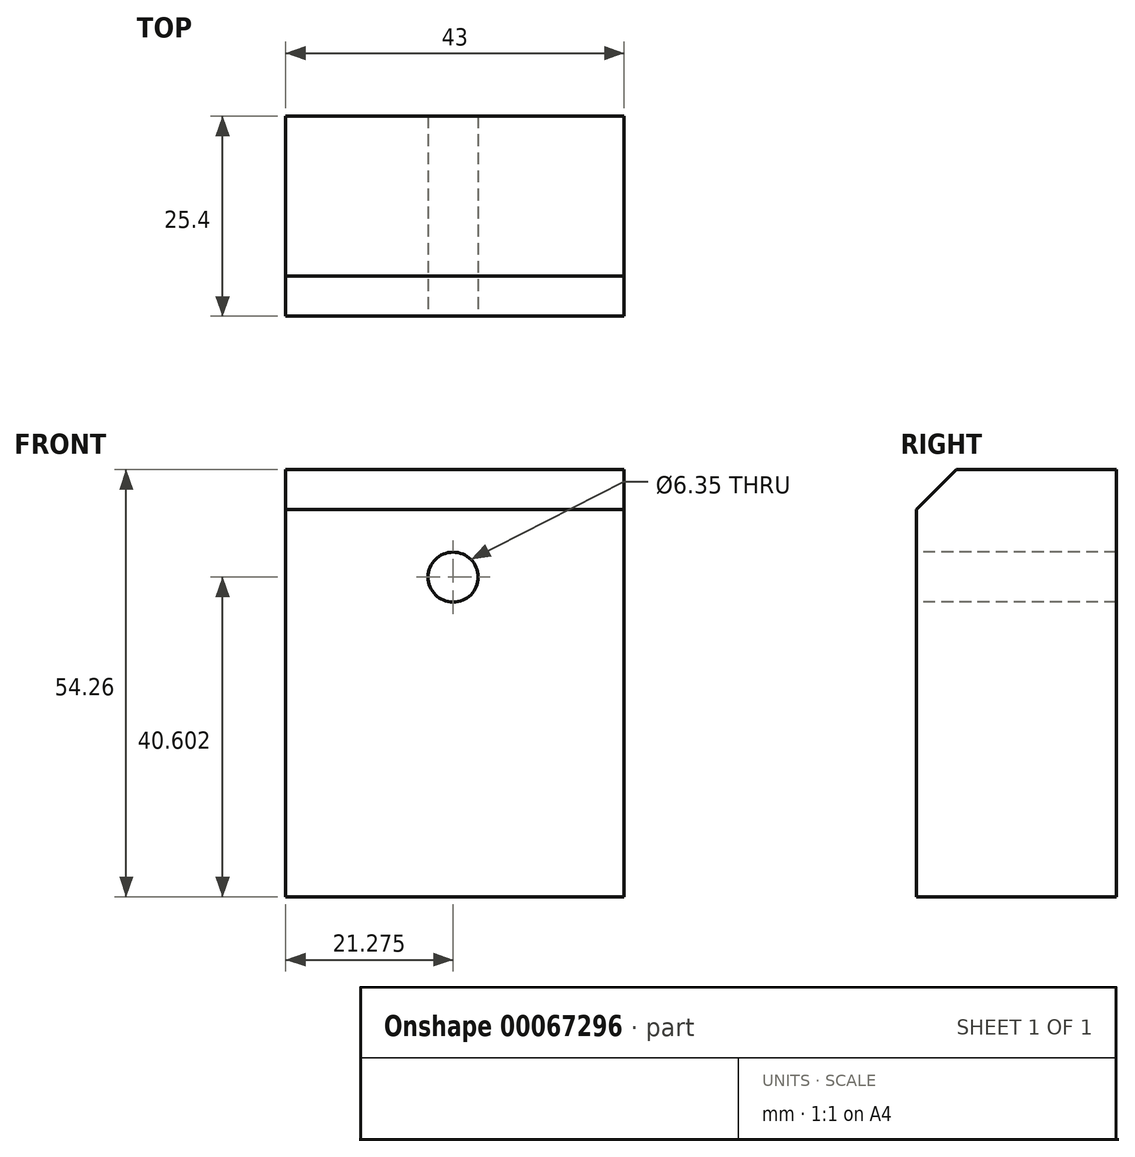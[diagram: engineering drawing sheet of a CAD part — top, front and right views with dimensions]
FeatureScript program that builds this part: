
annotation { "Feature Type Name" : "Feature", "Feature Type Description" : "" }
export const myFeature = defineFeature(function(context is Context, id is Id, definition is map)
    precondition{}
    {
        {
            var Q0;
            Q0=qCreatedBy(makeId("Front.planeOp"),FACE);
            var sketch = newSketch(context, id + "F0", { "sketchPlane" : qUnion([Q0])});
            skLineSegment(sketch, "E0.bottom", {"start": v(-13.34, 26.21) * mm, "end": v(29.66, 26.21) * mm});
            skLineSegment(sketch, "E0.top", {"start": v(-13.34, -28.05) * mm, "end": v(29.66, -28.05) * mm});
            skLineSegment(sketch, "E0.left", {"start": v(-13.34, 26.21) * mm, "end": v(-13.34, -28.05) * mm});
            skLineSegment(sketch, "E0.right", {"start": v(29.66, 26.21) * mm, "end": v(29.66, -28.05) * mm});
            skSolve(sketch);
        }
        {
            var Q0;
            Q0=makeQuery(id+"F0.imprint","IMPRINT",FACE,{"disambiguationData":[TD([[makeQuery(id+"F0.imprint","IMPRINT",EDGE,{"derivedFrom":sQuery(id+"F0.wireOp",EDGE,"E0.bottom")}),-1.0]])]});
            extrude(context, id + "F1", {"entities" : qUnion([Q0]), "depth" : 25.4 * mm});
        }
        {
            var Q0;
            Q0=makeQuery(id+"F1.opExtrude","CAP_FACE",FACE,{"disambiguationData":[OSD([sQuery(id+"F0.wireOp",EDGE,"E0.bottom"),sQuery(id+"F0.wireOp",EDGE,"E0.top"),sQuery(id+"F0.wireOp",EDGE,"E0.left"),sQuery(id+"F0.wireOp",EDGE,"E0.right")])],"isStart":false});
            var sketch = newSketch(context, id + "F2", { "sketchPlane" : qUnion([Q0])});
            skCircle(sketch, "E1", {"center": v(7.93, 12.55) * mm, "radius": 6.27 * mm});
            skSolve(sketch);
        }
        {
            var Q0;
            Q0=sQuery(id+"F2.wireOp",VERTEX,"E1.center");
            var Q1;
            Q1=makeQuery(id+"F1.opExtrude","SWEPT_BODY",BODY,{"disambiguationData":[OSD([sQuery(id+"F0.wireOp",EDGE,"E0.bottom"),sQuery(id+"F0.wireOp",EDGE,"E0.top"),sQuery(id+"F0.wireOp",EDGE,"E0.left"),sQuery(id+"F0.wireOp",EDGE,"E0.right")])]});
            hole(context, id + "F3", {"style" : HoleStyle.SIMPLE, "holeDiameter" : 6.35 * mm, "endStyle" : HoleEndStyle.THROUGH, "locations" : qUnion([Q0]), "scope" : qUnion([Q1])});
        }
        {
            var Q0;
            Q0=qCreatedBy(makeId("Front.planeOp"),FACE);
            var sketch = newSketch(context, id + "F4", { "sketchPlane" : qUnion([Q0])});
            skCircle(sketch, "E2", {"center": v(-59.33, 46.14) * mm, "radius": 11.37 * mm});
            skSolve(sketch);
        }
        {
            var Q0;
            Q0=sQuery(id+"F4.wireOp",EDGE,"E2");
            extrude(context, id + "F5", {"bodyType" : ToolBodyType.SURFACE, "surfaceEntities" : qUnion([Q0]), "depth" : 76.2 * mm});
        }
        {
            var Q0;
            Q0=makeQuery(id+"F1.opExtrude","CAP_EDGE",EDGE,{"disambiguationData":[OSD([sQuery(id+"F0.wireOp",EDGE,"E0.bottom")])],"isStart":false});
            chamfer(context, id + "F6", {"entities" : qUnion([Q0]), "width" : 5.08 * mm, "tangentPropagation" : true});
        }
    });
